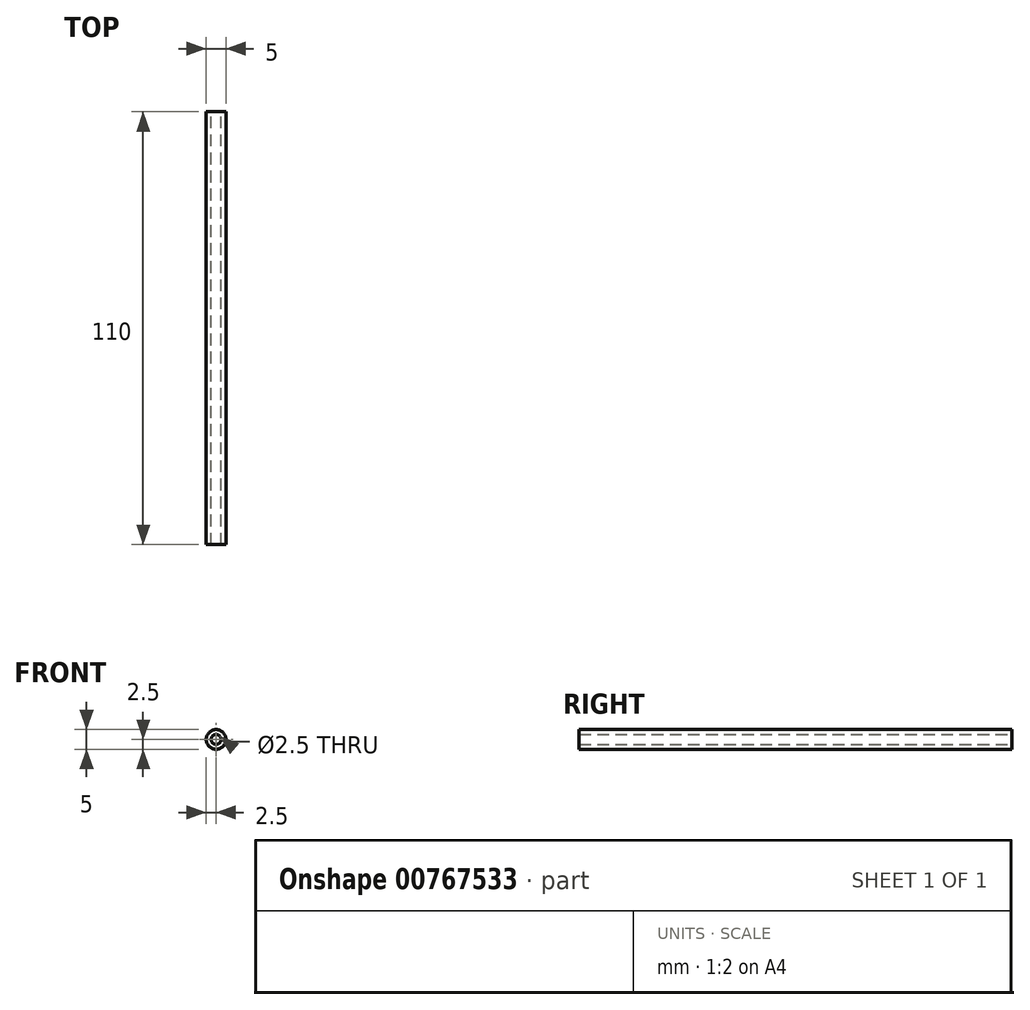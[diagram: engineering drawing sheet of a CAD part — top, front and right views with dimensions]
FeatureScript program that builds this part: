
annotation { "Feature Type Name" : "Feature", "Feature Type Description" : "" }
export const myFeature = defineFeature(function(context is Context, id is Id, definition is map)
    precondition{}
    {
        {
            var Q0;
            Q0=qCreatedBy(makeId("Front.planeOp"),FACE);
            var sketch = newSketch(context, id + "F0", { "sketchPlane" : qUnion([Q0])});
            skCircle(sketch, "E0", {"center": v(0, 0) * mm, "radius": 2.5 * mm});
            skCircle(sketch, "E1", {"center": v(0, 0) * mm, "radius": 1.25 * mm});
            skSolve(sketch);
        }
        {
            var Q0;
            Q0=makeQuery(id+"F0.imprint","IMPRINT",FACE,{"disambiguationData":[TD([[makeQuery(id+"F0.imprint","IMPRINT",EDGE,{"derivedFrom":sQuery(id+"F0.wireOp",EDGE,"E0")}),1.0]])]});
            extrude(context, id + "F1", {"entities" : qUnion([Q0]), "endBound" : BoundingType.SYMMETRIC, "depth" : 110 * mm, "offsetDistance" : 25 * mm});
        }
    });
